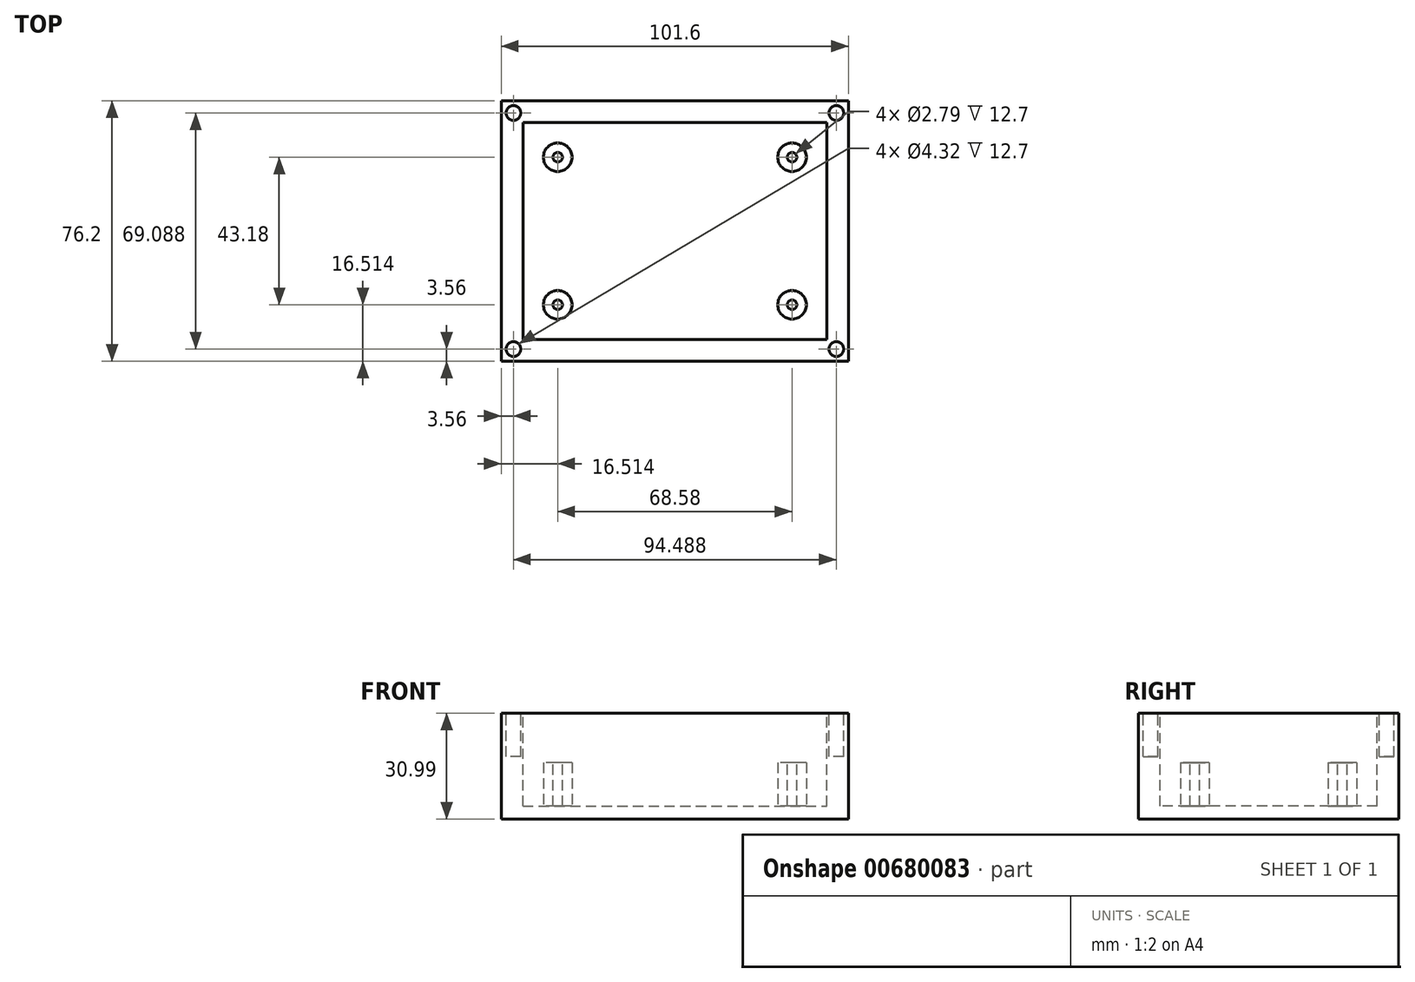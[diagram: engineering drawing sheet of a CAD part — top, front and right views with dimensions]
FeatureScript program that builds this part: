
annotation { "Feature Type Name" : "Feature", "Feature Type Description" : "" }
export const myFeature = defineFeature(function(context is Context, id is Id, definition is map)
    precondition{}
    {
        {
            var Q0;
            Q0=qCreatedBy(makeId("Top.planeOp"),FACE);
            var sketch = newSketch(context, id + "F0", { "sketchPlane" : qUnion([Q0])});
            skLineSegment(sketch, "E0.bottom", {"start": v(-90.8, 57.1) * mm, "end": v(10.8, 57.1) * mm});
            skLineSegment(sketch, "E0.top", {"start": v(-90.8, -19.1) * mm, "end": v(10.8, -19.1) * mm});
            skLineSegment(sketch, "E0.left", {"start": v(-90.8, 57.1) * mm, "end": v(-90.8, -19.1) * mm});
            skLineSegment(sketch, "E0.right", {"start": v(10.8, 57.1) * mm, "end": v(10.8, -19.1) * mm});
            skSolve(sketch);
        }
        {
            var Q0;
            Q0=makeQuery(id+"F0.imprint","IMPRINT",FACE,{"disambiguationData":[TD([[makeQuery(id+"F0.imprint","IMPRINT",EDGE,{"derivedFrom":sQuery(id+"F0.wireOp",EDGE,"E0.bottom")}),-1.0]])]});
            extrude(context, id + "F1", {"entities" : qUnion([Q0]), "depth" : 30.99 * mm, "offsetDistance" : 25.4 * mm});
        }
        {
            var Q0;
            Q0=makeQuery(id+"F1.opExtrude","CAP_FACE",FACE,{"disambiguationData":[OSD([sQuery(id+"F0.wireOp",EDGE,"E0.bottom"),sQuery(id+"F0.wireOp",EDGE,"E0.top"),sQuery(id+"F0.wireOp",EDGE,"E0.left"),sQuery(id+"F0.wireOp",EDGE,"E0.right")])],"isStart":false});
            var sketch = newSketch(context, id + "F2", { "sketchPlane" : qUnion([Q0])});
            skLineSegment(sketch, "E1.bottom", {"start": v(-84.46, 50.75) * mm, "end": v(4.44, 50.75) * mm});
            skLineSegment(sketch, "E1.top", {"start": v(-84.46, -12.75) * mm, "end": v(4.44, -12.75) * mm});
            skLineSegment(sketch, "E1.left", {"start": v(-84.46, 50.75) * mm, "end": v(-84.46, -12.75) * mm});
            skLineSegment(sketch, "E1.right", {"start": v(4.44, 50.75) * mm, "end": v(4.44, -12.75) * mm});
            skPoint(sketch, "E1.middle", {"position": v(-40, 19) * mm});
            skPoint(sketch, "E1.middle.positionSnap0", {"position": v(-90.8, 19) * mm});
            skPoint(sketch, "E1.middle.positionSnap1", {"position": v(-40, -19.1) * mm});
            skPoint(sketch, "E1.centerSnap0", {"position": v(-90.8, 19) * mm});
            skPoint(sketch, "E1.centerSnap1", {"position": v(-40, -19.1) * mm});
            skSolve(sketch);
        }
        {
            var Q0;
            Q0=makeQuery(id+"F2.imprint","IMPRINT",FACE,{"disambiguationData":[TD([[makeQuery(id+"F2.imprint","IMPRINT",EDGE,{"derivedFrom":sQuery(id+"F2.wireOp",EDGE,"E1.bottom")}),-1.0]])]});
            extrude(context, id + "F3", {"entities" : qUnion([Q0]), "operationType" : NewBodyOperationType.REMOVE, "oppositeDirection" : true, "depth" : 27.18 * mm, "offsetDistance" : 25.4 * mm});
        }
        {
            var Q0;
            Q0=makeQuery(id+"F3.boolean.opBoolean","COPY",FACE,{"derivedFrom":makeQuery(id+"F3.opExtrude","CAP_FACE",FACE,{"disambiguationData":[OSD([sQuery(id+"F2.wireOp",EDGE,"E1.bottom"),sQuery(id+"F2.wireOp",EDGE,"E1.top"),sQuery(id+"F2.wireOp",EDGE,"E1.left"),sQuery(id+"F2.wireOp",EDGE,"E1.right")])],"isStart":false})});
            var sketch = newSketch(context, id + "F4", { "sketchPlane" : qUnion([Q0])});
            skCircle(sketch, "E2", {"center": v(-74.3, 40.6) * mm, "radius": 4.2 * mm});
            skCircle(sketch, "E3", {"center": v(-5.72, 40.6) * mm, "radius": 4.2 * mm});
            skCircle(sketch, "E4", {"center": v(-74.3, -2.59) * mm, "radius": 4.2 * mm});
            skCircle(sketch, "E5", {"center": v(-5.72, -2.59) * mm, "radius": 4.2 * mm});
            skSolve(sketch);
        }
        {
            var Q0;
            Q0=makeQuery(id+"F4.imprint","IMPRINT",FACE,{"disambiguationData":[TD([[makeQuery(id+"F4.imprint","IMPRINT",EDGE,{"derivedFrom":sQuery(id+"F4.wireOp",EDGE,"E2")}),1.0]])]});
            var Q1;
            Q1=makeQuery(id+"F4.imprint","IMPRINT",FACE,{"disambiguationData":[TD([[makeQuery(id+"F4.imprint","IMPRINT",EDGE,{"derivedFrom":sQuery(id+"F4.wireOp",EDGE,"E3")}),1.0]])]});
            var Q2;
            Q2=makeQuery(id+"F4.imprint","IMPRINT",FACE,{"disambiguationData":[TD([[makeQuery(id+"F4.imprint","IMPRINT",EDGE,{"derivedFrom":sQuery(id+"F4.wireOp",EDGE,"E5")}),1.0]])]});
            var Q3;
            Q3=makeQuery(id+"F4.imprint","IMPRINT",FACE,{"disambiguationData":[TD([[makeQuery(id+"F4.imprint","IMPRINT",EDGE,{"derivedFrom":sQuery(id+"F4.wireOp",EDGE,"E4")}),1.0]])]});
            extrude(context, id + "F5", {"entities" : qUnion([Q0, Q1, Q2, Q3]), "operationType" : NewBodyOperationType.ADD, "depth" : 12.7 * mm, "offsetDistance" : 25.4 * mm});
        }
        {
            var Q0;
            Q0=makeQuery(id+"F5.opExtrude","CAP_FACE",FACE,{"disambiguationData":[OSD([sQuery(id+"F4.wireOp",EDGE,"E2")])],"isStart":false});
            var sketch = newSketch(context, id + "F6", { "sketchPlane" : qUnion([Q0])});
            skCircle(sketch, "E6", {"center": v(-74.3, 40.6) * mm, "radius": 1.4 * mm});
            skSolve(sketch);
        }
        {
            var Q0;
            Q0=makeQuery(id+"F5.opExtrude","CAP_FACE",FACE,{"disambiguationData":[OSD([sQuery(id+"F4.wireOp",EDGE,"E3")])],"isStart":false});
            var sketch = newSketch(context, id + "F7", { "sketchPlane" : qUnion([Q0])});
            skCircle(sketch, "E7", {"center": v(-5.72, 40.6) * mm, "radius": 1.4 * mm});
            skSolve(sketch);
        }
        {
            var Q0;
            Q0=makeQuery(id+"F5.opExtrude","CAP_FACE",FACE,{"disambiguationData":[OSD([sQuery(id+"F4.wireOp",EDGE,"E4")])],"isStart":false});
            var sketch = newSketch(context, id + "F8", { "sketchPlane" : qUnion([Q0])});
            skCircle(sketch, "E8", {"center": v(-74.3, -2.59) * mm, "radius": 1.4 * mm});
            skSolve(sketch);
        }
        {
            var Q0;
            Q0=makeQuery(id+"F5.opExtrude","CAP_FACE",FACE,{"disambiguationData":[OSD([sQuery(id+"F4.wireOp",EDGE,"E5")])],"isStart":false});
            var sketch = newSketch(context, id + "F9", { "sketchPlane" : qUnion([Q0])});
            skCircle(sketch, "E9", {"center": v(-5.72, -2.59) * mm, "radius": 1.4 * mm});
            skSolve(sketch);
        }
        {
            var Q0;
            Q0=makeQuery(id+"F6.imprint","IMPRINT",FACE,{"disambiguationData":[TD([[makeQuery(id+"F6.imprint","IMPRINT",EDGE,{"derivedFrom":sQuery(id+"F6.wireOp",EDGE,"E6")}),1.0]])]});
            var Q1;
            Q1=makeQuery(id+"F8.imprint","IMPRINT",FACE,{"disambiguationData":[TD([[makeQuery(id+"F8.imprint","IMPRINT",EDGE,{"derivedFrom":sQuery(id+"F8.wireOp",EDGE,"E8")}),1.0]])]});
            var Q2;
            Q2=makeQuery(id+"F9.imprint","IMPRINT",FACE,{"disambiguationData":[TD([[makeQuery(id+"F9.imprint","IMPRINT",EDGE,{"derivedFrom":sQuery(id+"F9.wireOp",EDGE,"E9")}),1.0]])]});
            var Q3;
            Q3=makeQuery(id+"F7.imprint","IMPRINT",FACE,{"disambiguationData":[TD([[makeQuery(id+"F7.imprint","IMPRINT",EDGE,{"derivedFrom":sQuery(id+"F7.wireOp",EDGE,"E7")}),1.0]])]});
            extrude(context, id + "F10", {"entities" : qUnion([Q0, Q1, Q2, Q3]), "operationType" : NewBodyOperationType.REMOVE, "oppositeDirection" : true, "depth" : 12.7 * mm, "offsetDistance" : 25.4 * mm});
        }
        {
            var Q0;
            Q0=makeQuery(id+"F1.opExtrude","CAP_FACE",FACE,{"disambiguationData":[OSD([sQuery(id+"F0.wireOp",EDGE,"E0.bottom"),sQuery(id+"F0.wireOp",EDGE,"E0.top"),sQuery(id+"F0.wireOp",EDGE,"E0.left"),sQuery(id+"F0.wireOp",EDGE,"E0.right")])],"isStart":false});
            var sketch = newSketch(context, id + "F11", { "sketchPlane" : qUnion([Q0])});
            skCircle(sketch, "E10", {"center": v(-87.25, 53.55) * mm, "radius": 2.16 * mm});
            skCircle(sketch, "E11", {"center": v(-87.25, -15.54) * mm, "radius": 2.16 * mm});
            skCircle(sketch, "E12", {"center": v(7.24, 53.55) * mm, "radius": 2.16 * mm});
            skCircle(sketch, "E13", {"center": v(7.24, -15.54) * mm, "radius": 2.16 * mm});
            skSolve(sketch);
        }
        {
            var Q0;
            Q0=makeQuery(id+"F11.imprint","IMPRINT",FACE,{"disambiguationData":[TD([[makeQuery(id+"F11.imprint","IMPRINT",EDGE,{"derivedFrom":sQuery(id+"F11.wireOp",EDGE,"E10")}),1.0]])]});
            var Q1;
            Q1=makeQuery(id+"F11.imprint","IMPRINT",FACE,{"disambiguationData":[TD([[makeQuery(id+"F11.imprint","IMPRINT",EDGE,{"derivedFrom":sQuery(id+"F11.wireOp",EDGE,"E11")}),1.0]])]});
            var Q2;
            Q2=makeQuery(id+"F11.imprint","IMPRINT",FACE,{"disambiguationData":[TD([[makeQuery(id+"F11.imprint","IMPRINT",EDGE,{"derivedFrom":sQuery(id+"F11.wireOp",EDGE,"E13")}),1.0]])]});
            var Q3;
            Q3=makeQuery(id+"F11.imprint","IMPRINT",FACE,{"disambiguationData":[TD([[makeQuery(id+"F11.imprint","IMPRINT",EDGE,{"derivedFrom":sQuery(id+"F11.wireOp",EDGE,"E12")}),1.0]])]});
            extrude(context, id + "F12", {"entities" : qUnion([Q0, Q1, Q2, Q3]), "operationType" : NewBodyOperationType.REMOVE, "oppositeDirection" : true, "depth" : 12.7 * mm, "offsetDistance" : 25.4 * mm});
        }
    });
